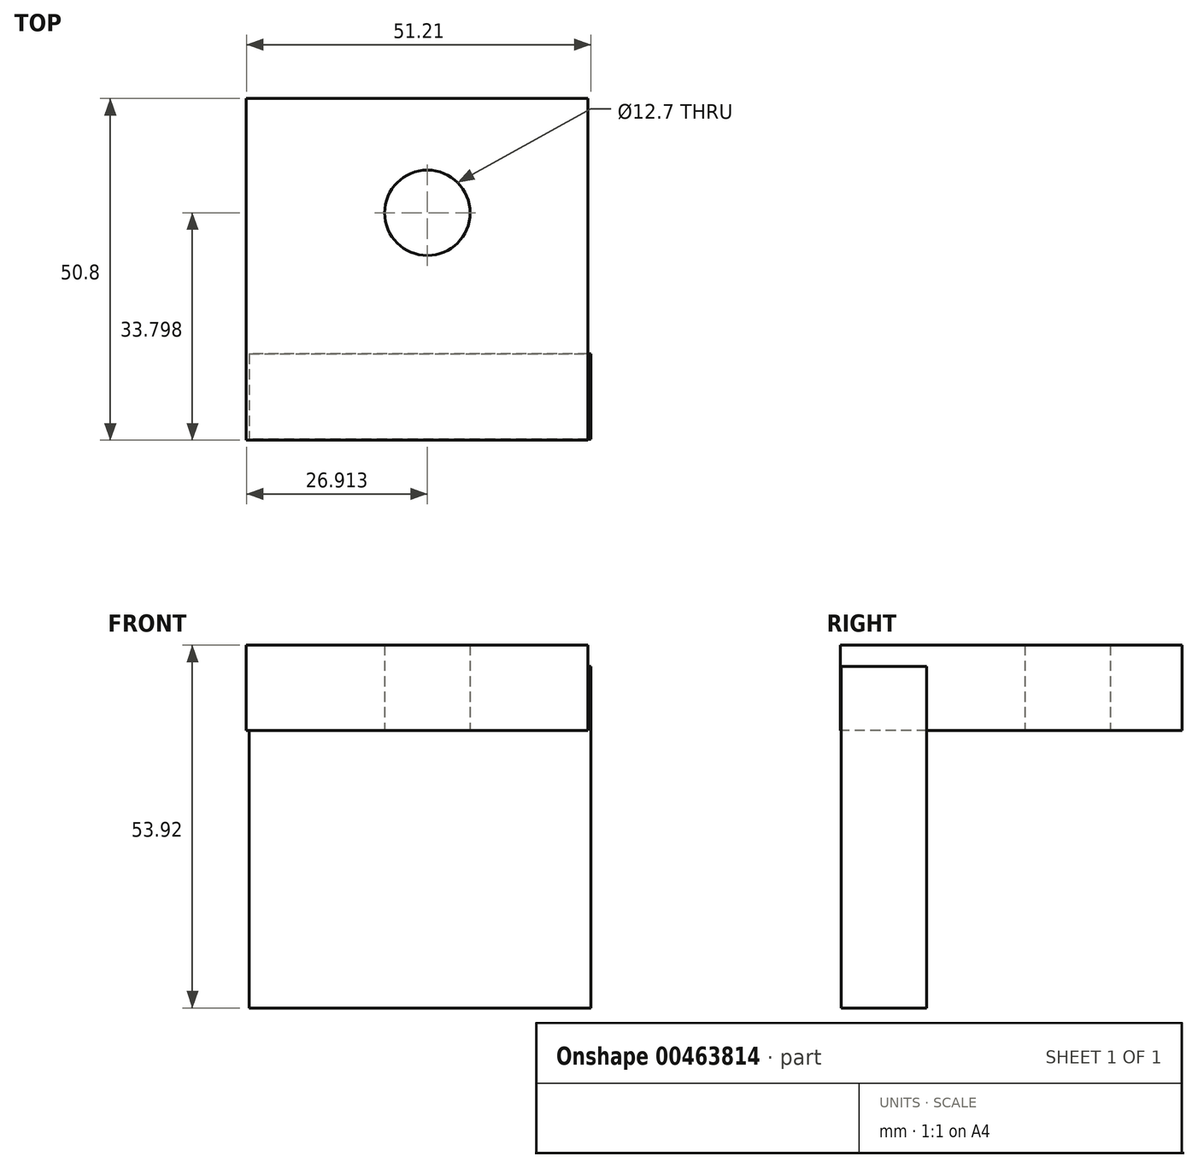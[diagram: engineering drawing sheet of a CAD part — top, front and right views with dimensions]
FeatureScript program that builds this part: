
annotation { "Feature Type Name" : "Feature", "Feature Type Description" : "" }
export const myFeature = defineFeature(function(context is Context, id is Id, definition is map)
    precondition{}
    {
        {
            var Q0;
            Q0=qCreatedBy(makeId("Front.planeOp"),FACE);
            var sketch = newSketch(context, id + "F0", { "sketchPlane" : qUnion([Q0])});
            skLineSegment(sketch, "E0.bottom", {"start": v(-24.02, 9.58) * mm, "end": v(26.78, 9.58) * mm});
            skLineSegment(sketch, "E0.top", {"start": v(-24.02, -41.22) * mm, "end": v(26.78, -41.22) * mm});
            skLineSegment(sketch, "E0.left", {"start": v(-24.02, 9.58) * mm, "end": v(-24.02, -41.22) * mm});
            skLineSegment(sketch, "E0.right", {"start": v(26.78, 9.58) * mm, "end": v(26.78, -41.22) * mm});
            skSolve(sketch);
        }
        {
            var Q0;
            Q0=makeQuery(id+"F0.imprint","IMPRINT",FACE,{"disambiguationData":[TD([[makeQuery(id+"F0.imprint","IMPRINT",EDGE,{"derivedFrom":sQuery(id+"F0.wireOp",EDGE,"E0.bottom")}),-1.0]])]});
            extrude(context, id + "F1", {"entities" : qUnion([Q0]), "depth" : 12.7 * mm});
        }
        {
            var Q0;
            Q0=qCreatedBy(makeId("Top.planeOp"),FACE);
            var sketch = newSketch(context, id + "F2", { "sketchPlane" : qUnion([Q0])});
            skLineSegment(sketch, "E1.bottom", {"start": v(-24.43, -12.83) * mm, "end": v(26.37, -12.83) * mm});
            skLineSegment(sketch, "E1.top", {"start": v(-24.43, 37.97) * mm, "end": v(26.37, 37.97) * mm});
            skLineSegment(sketch, "E1.left", {"start": v(-24.43, -12.83) * mm, "end": v(-24.43, 37.97) * mm});
            skLineSegment(sketch, "E1.right", {"start": v(26.37, -12.83) * mm, "end": v(26.37, 37.97) * mm});
            skSolve(sketch);
        }
        {
            var Q0;
            Q0 = qSketchRegion(id + "F2", true);
            extrude(context, id + "F3", {"entities" : qUnion([Q0]), "operationType" : NewBodyOperationType.ADD, "depth" : 12.7 * mm});
        }
        {
            var Q0;
            Q0=makeQuery(id+"F2.imprint","IMPRINT",FACE,{"disambiguationData":[TD([[makeQuery(id+"F2.imprint","IMPRINT",EDGE,{"derivedFrom":sQuery(id+"F2.wireOp",EDGE,"E1.bottom")}),1.0]])]});
            var sketch = newSketch(context, id + "F4", { "sketchPlane" : qUnion([Q0])});
            skCircle(sketch, "E2", {"center": v(2.48, 20.97) * mm, "radius": 6.35 * mm});
            skSolve(sketch);
        }
        {
            var Q0;
            Q0 = qSketchRegion(id + "F4", true);
            extrude(context, id + "F5", {"entities" : qUnion([Q0]), "operationType" : NewBodyOperationType.REMOVE, "depth" : 25.4 * mm});
        }
    });
